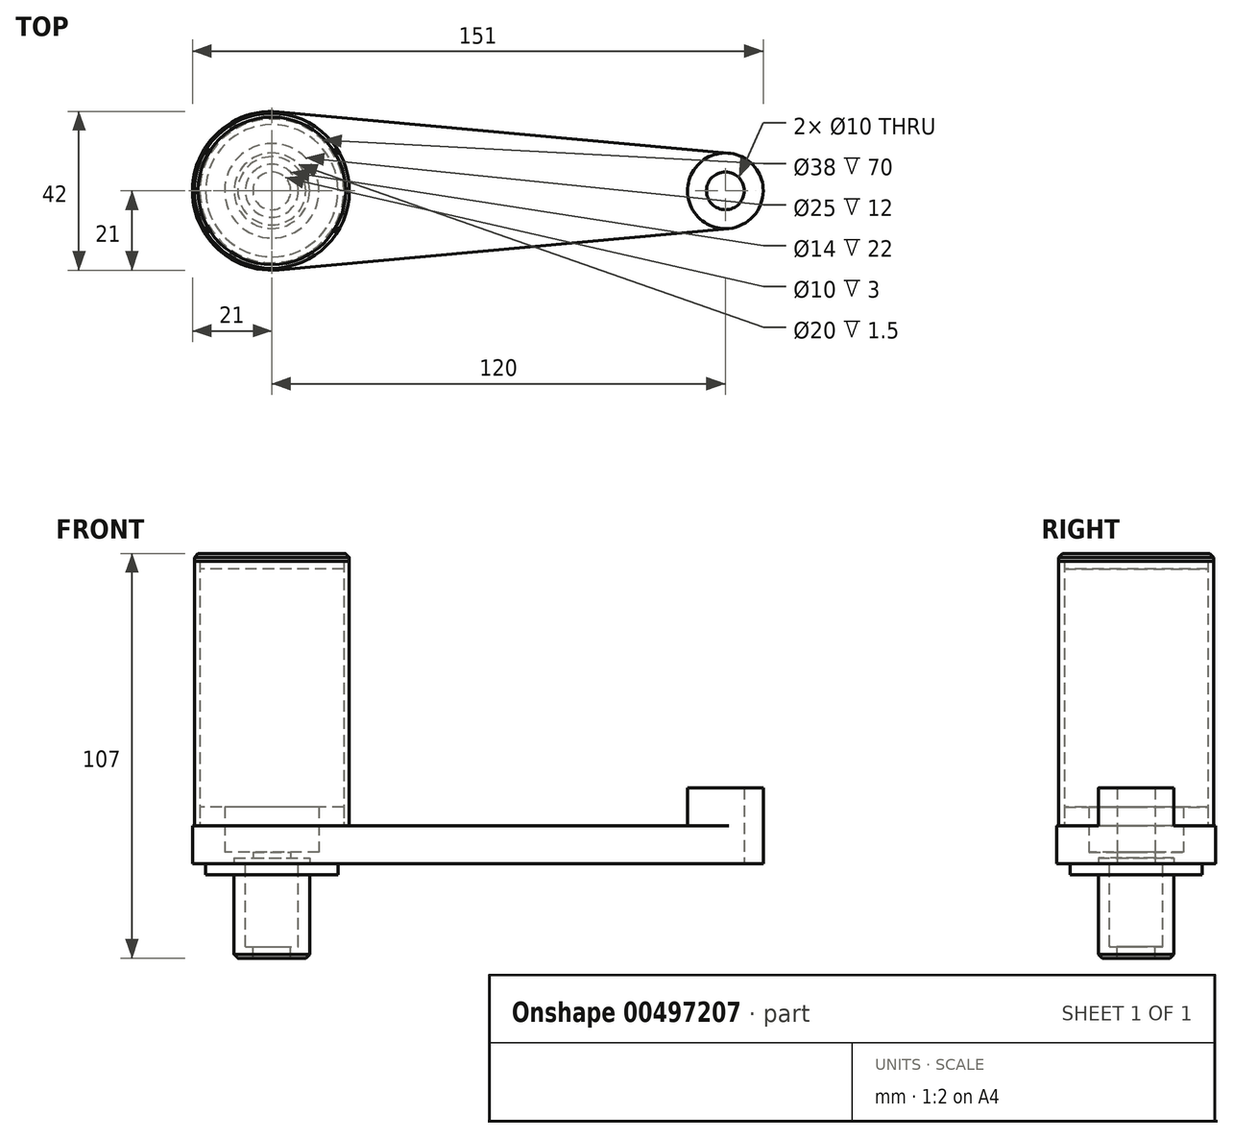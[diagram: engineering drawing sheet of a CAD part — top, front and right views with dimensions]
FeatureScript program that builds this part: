
annotation { "Feature Type Name" : "Feature", "Feature Type Description" : "" }
export const myFeature = defineFeature(function(context is Context, id is Id, definition is map)
    precondition{}
    {
        {
            var Q0;
            Q0=qCreatedBy(makeId("Top.planeOp"),FACE);
            var sketch = newSketch(context, id + "F0", { "sketchPlane" : qUnion([Q0])});
            skCircle(sketch, "E0", {"center": v(0, 0) * mm, "radius": 5 * mm});
            skCircle(sketch, "E1", {"center": v(0, 0) * mm, "radius": 10 * mm});
            skCircle(sketch, "E2", {"center": v(-120, 0) * mm, "radius": 5 * mm});
            skCircle(sketch, "E3", {"center": v(-120, 0) * mm, "radius": 21 * mm});
            skCircle(sketch, "E4", {"center": v(-120, 0) * mm, "radius": 12.5 * mm});
            skLineSegment(sketch, "E5", {"start": v(-119.26, 21.02) * mm, "end": v(0.92, 9.96) * mm});
            skLineSegment(sketch, "E6", {"start": v(-119.26, -21.02) * mm, "end": v(0.92, -9.96) * mm});
            skCircle(sketch, "E7", {"center": v(-120, 0) * mm, "radius": 19 * mm});
            skSolve(sketch);
        }
        {
            var Q0;
            {var subQ0=sQuery(id+"F0.wireOp",EDGE,"E5");var subQ1=sQuery(id+"F0.wireOp",EDGE,"E1");var subQ2=makeQuery(id+"F0.imprint","INTERSECT",VERTEX,{"derivedFrom":[subQ1,subQ0]});Q0=makeQuery(id+"F0.imprint","IMPRINT",FACE,{"disambiguationData":[TD([[makeQuery(id+"F0.imprint","IMPRINT",EDGE,{"disambiguationData":[TD([[subQ2,-1.0]])],"derivedFrom":subQ1}),-1.0]])]});}
            var Q1;
            Q1=makeQuery(id+"F0.imprint","IMPRINT",FACE,{"disambiguationData":[TD([[makeQuery(id+"F0.imprint","IMPRINT",EDGE,{"derivedFrom":sQuery(id+"F0.wireOp",EDGE,"E7")}),-1.0]])]});
            extrude(context, id + "F1", {"entities" : qUnion([Q0, Q1]), "depth" : 10 * mm});
        }
        {
            var Q0;
            Q0=makeQuery(id+"F0.imprint","IMPRINT",FACE,{"disambiguationData":[TD([[makeQuery(id+"F0.imprint","IMPRINT",EDGE,{"derivedFrom":sQuery(id+"F0.wireOp",EDGE,"E0")}),-1.0]])]});
            extrude(context, id + "F2", {"entities" : qUnion([Q0]), "operationType" : NewBodyOperationType.ADD, "depth" : 20 * mm});
        }
        {
            var Q0;
            Q0=makeQuery(id+"F0.imprint","IMPRINT",FACE,{"disambiguationData":[TD([[makeQuery(id+"F0.imprint","IMPRINT",EDGE,{"derivedFrom":sQuery(id+"F0.wireOp",EDGE,"E4")}),-1.0]])]});
            extrude(context, id + "F3", {"entities" : qUnion([Q0]), "operationType" : NewBodyOperationType.ADD, "depth" : 15 * mm});
        }
        {
            var Q0;
            {var subQ0=sQuery(id+"F0.wireOp",EDGE,"E7");var subQ1=sQuery(id+"F0.wireOp",EDGE,"E1");Q0=makeQuery(id+"F3.boolean.opBoolean","MERGE",FACE,{"derivedFrom":[makeQuery(id+"F2.boolean.opBoolean","MERGE",FACE,{"derivedFrom":[makeQuery(id+"F1.opExtrude","CAP_FACE",FACE,{"disambiguationData":[OSD([subQ1,sQuery(id+"F0.wireOp",EDGE,"E3"),sQuery(id+"F0.wireOp",EDGE,"E5"),sQuery(id+"F0.wireOp",EDGE,"E6"),subQ0])],"isStart":true}),makeQuery(id+"F2.opExtrude","CAP_FACE",FACE,{"disambiguationData":[OSD([sQuery(id+"F0.wireOp",EDGE,"E0"),subQ1])],"isStart":true})]}),makeQuery(id+"F3.opExtrude","CAP_FACE",FACE,{"disambiguationData":[OSD([sQuery(id+"F0.wireOp",EDGE,"E4"),subQ0])],"isStart":true})]});}
            var sketch = newSketch(context, id + "F4", { "sketchPlane" : qUnion([Q0])});
            skCircle(sketch, "E8", {"center": v(-120, 0) * mm, "radius": 17.5 * mm});
            skCircle(sketch, "E9", {"center": v(-120, 0) * mm, "radius": 10 * mm});
            skCircle(sketch, "E10", {"center": v(-120, 0) * mm, "radius": 7 * mm});
            skCircle(sketch, "E11", {"center": v(-120, 0) * mm, "radius": 5 * mm});
            skSolve(sketch);
        }
        {
            var Q0;
            Q0 = qSketchRegion(id + "F4", true);
            extrude(context, id + "F5", {"entities" : qUnion([Q0]), "depth" : 3 * mm});
        }
        {
            var Q0;
            Q0=makeQuery(id+"F4.imprint","IMPRINT",FACE,{"disambiguationData":[TD([[makeQuery(id+"F4.imprint","IMPRINT",EDGE,{"derivedFrom":sQuery(id+"F4.wireOp",EDGE,"E9")}),1.0]])]});
            extrude(context, id + "F6", {"entities" : qUnion([Q0]), "operationType" : NewBodyOperationType.ADD, "depth" : 25 * mm});
        }
        {
            var Q0;
            Q0=makeQuery(id+"F4.imprint","IMPRINT",FACE,{"disambiguationData":[TD([[makeQuery(id+"F4.imprint","IMPRINT",EDGE,{"derivedFrom":sQuery(id+"F4.wireOp",EDGE,"E10")}),1.0]])]});
            extrude(context, id + "F7", {"entities" : qUnion([Q0]), "operationType" : NewBodyOperationType.ADD, "depth" : 25 * mm, "hasSecondDirection" : true, "secondDirectionOppositeDirection" : false, "secondDirectionDepth" : 22 * mm});
        }
        {
            var Q0;
            Q0=makeQuery(id+"F6.opExtrude","CAP_EDGE",EDGE,{"disambiguationData":[OSD([sQuery(id+"F4.wireOp",EDGE,"E9")])],"isStart":false});
            chamfer(context, id + "F8", {"entities" : qUnion([Q0]), "width" : 1 * mm, "tangentPropagation" : true});
        }
        {
            var Q0;
            Q0=makeQuery(id+"F1.opExtrude","CAP_FACE",FACE,{"disambiguationData":[OSD([sQuery(id+"F0.wireOp",EDGE,"E1"),sQuery(id+"F0.wireOp",EDGE,"E3"),sQuery(id+"F0.wireOp",EDGE,"E5"),sQuery(id+"F0.wireOp",EDGE,"E6"),sQuery(id+"F0.wireOp",EDGE,"E7")])],"isStart":false});
            var sketch = newSketch(context, id + "F9", { "sketchPlane" : qUnion([Q0])});
            skCircle(sketch, "E12", {"center": v(-120, 0) * mm, "radius": 20.5 * mm});
            skCircle(sketch, "E13", {"center": v(-120, 0) * mm, "radius": 19 * mm});
            skSolve(sketch);
        }
        {
            var Q0;
            Q0 = qSketchRegion(id + "F9", true);
            extrude(context, id + "F10", {"entities" : qUnion([Q0]), "depth" : 70 * mm});
        }
        {
            var Q0;
            Q0=makeQuery(id+"F1.opExtrude","SWEPT_BODY",BODY,{"disambiguationData":[OSD([sQuery(id+"F0.wireOp",EDGE,"E1"),sQuery(id+"F0.wireOp",EDGE,"E3"),sQuery(id+"F0.wireOp",EDGE,"E5"),sQuery(id+"F0.wireOp",EDGE,"E6"),sQuery(id+"F0.wireOp",EDGE,"E7")])]});
            var Q1;
            Q1=makeQuery(id+"F5.opExtrude","SWEPT_BODY",BODY,{"disambiguationData":[OSD([sQuery(id+"F4.wireOp",EDGE,"E8"),sQuery(id+"F4.wireOp",EDGE,"E9")])]});
            booleanBodies(context, id + "F11", {"operationType" : BooleanOperationType.SUBTRACTION, "tools" : qUnion([Q0]), "targets" : qUnion([Q1]), "keepTools" : true});
        }
        {
            var Q0;
            Q0=makeQuery(id+"F9.imprint","IMPRINT",FACE,{"disambiguationData":[TD([[makeQuery(id+"F9.imprint","IMPRINT",EDGE,{"derivedFrom":sQuery(id+"F9.wireOp",EDGE,"E12")}),1.0]])]});
            var Q1;
            Q1=makeQuery(id+"F9.imprint","IMPRINT",FACE,{"disambiguationData":[TD([[makeQuery(id+"F9.imprint","IMPRINT",EDGE,{"derivedFrom":sQuery(id+"F9.wireOp",EDGE,"E13")}),1.0]])]});
            extrude(context, id + "F12", {"entities" : qUnion([Q0, Q1]), "depth" : 72 * mm, "hasSecondDirection" : true, "secondDirectionOppositeDirection" : false, "secondDirectionDepth" : 68 * mm});
        }
        {
            var Q0;
            Q0=makeQuery(id+"F10.opExtrude","SWEPT_BODY",BODY,{"disambiguationData":[OSD([sQuery(id+"F9.wireOp",EDGE,"E12"),sQuery(id+"F9.wireOp",EDGE,"E13")])]});
            var Q1;
            Q1=makeQuery(id+"F12.opExtrude","SWEPT_BODY",BODY,{"disambiguationData":[OSD([sQuery(id+"F9.wireOp",EDGE,"E12")])]});
            booleanBodies(context, id + "F13", {"operationType" : BooleanOperationType.SUBTRACTION, "tools" : qUnion([Q0]), "targets" : qUnion([Q1]), "keepTools" : true});
        }
        {
            var Q0;
            Q0=makeQuery(id+"F12.opExtrude","CAP_EDGE",EDGE,{"disambiguationData":[OSD([sQuery(id+"F9.wireOp",EDGE,"E12")])],"isStart":false});
            chamfer(context, id + "F14", {"entities" : qUnion([Q0]), "width" : 1 * mm, "tangentPropagation" : true});
        }
        {
            var Q0;
            Q0=makeQuery(id+"F4.imprint","IMPRINT",FACE,{"disambiguationData":[TD([[makeQuery(id+"F4.imprint","IMPRINT",EDGE,{"derivedFrom":sQuery(id+"F4.wireOp",EDGE,"E10")}),1.0]])]});
            var Q1;
            Q1=makeQuery(id+"F4.imprint","IMPRINT",FACE,{"disambiguationData":[TD([[makeQuery(id+"F4.imprint","IMPRINT",EDGE,{"derivedFrom":sQuery(id+"F4.wireOp",EDGE,"E9")}),1.0]])]});
            var Q2;
            Q2=makeQuery(id+"F4.imprint","IMPRINT",FACE,{"disambiguationData":[TD([[makeQuery(id+"F4.imprint","IMPRINT",EDGE,{"derivedFrom":sQuery(id+"F4.wireOp",EDGE,"E9")}),-1.0]])]});
            extrude(context, id + "F15", {"entities" : qUnion([Q0, Q1, Q2]), "operationType" : NewBodyOperationType.ADD, "oppositeDirection" : true, "depth" : 3 * mm});
        }
        {
            var Q0;
            Q0=makeQuery(id+"F4.imprint","IMPRINT",FACE,{"disambiguationData":[TD([[makeQuery(id+"F4.imprint","IMPRINT",EDGE,{"derivedFrom":sQuery(id+"F4.wireOp",EDGE,"E9")}),1.0]])]});
            var Q1;
            Q1=makeQuery(id+"F4.imprint","IMPRINT",FACE,{"disambiguationData":[TD([[makeQuery(id+"F4.imprint","IMPRINT",EDGE,{"derivedFrom":sQuery(id+"F4.wireOp",EDGE,"E10")}),1.0]])]});
            extrude(context, id + "F16", {"entities" : qUnion([Q0, Q1]), "operationType" : NewBodyOperationType.ADD, "oppositeDirection" : true, "depth" : 1.5 * mm});
        }
        {
            var Q0;
            Q0=makeQuery(id+"F4.imprint","IMPRINT",FACE,{"disambiguationData":[TD([[makeQuery(id+"F4.imprint","IMPRINT",EDGE,{"derivedFrom":sQuery(id+"F4.wireOp",EDGE,"E9")}),1.0]])]});
            var Q1;
            Q1=makeQuery(id+"F4.imprint","IMPRINT",FACE,{"disambiguationData":[TD([[makeQuery(id+"F4.imprint","IMPRINT",EDGE,{"derivedFrom":sQuery(id+"F4.wireOp",EDGE,"E10")}),1.0]])]});
            var Q2;
            Q2=makeQuery(id+"F4.imprint","IMPRINT",FACE,{"disambiguationData":[TD([[makeQuery(id+"F4.imprint","IMPRINT",EDGE,{"derivedFrom":sQuery(id+"F4.wireOp",EDGE,"E11")}),1.0]])]});
            extrude(context, id + "F17", {"entities" : qUnion([Q0, Q1, Q2]), "oppositeDirection" : true, "depth" : 1.5 * mm});
        }
        {
            var Q0;
            Q0=makeQuery(id+"F17.opExtrude","SWEPT_BODY",BODY,{"disambiguationData":[OSD([sQuery(id+"F4.wireOp",EDGE,"E9")])]});
            var Q1;
            Q1=makeQuery(id+"F1.opExtrude","SWEPT_BODY",BODY,{"disambiguationData":[OSD([sQuery(id+"F0.wireOp",EDGE,"E1"),sQuery(id+"F0.wireOp",EDGE,"E3"),sQuery(id+"F0.wireOp",EDGE,"E5"),sQuery(id+"F0.wireOp",EDGE,"E6"),sQuery(id+"F0.wireOp",EDGE,"E7")])]});
            booleanBodies(context, id + "F18", {"operationType" : BooleanOperationType.SUBTRACTION, "tools" : qUnion([Q0]), "targets" : qUnion([Q1])});
        }
    });
